# Revit family: Hitachi_RAS-70YHA4_RAS-80YHA4_1116
name_source: partatom
category: Mechanical Equipment
revit_build: Autodesk Revit 2013 (Build: 20120221_2030(x64)
units: mm (PartAtom-declared; Revit-internal decimal feet)

## types (2) — shared parameters
Depth = 250 mm  [stored 0.82021 ft]
Energy Star = Yes
Height = 300 mm
Manufacturer = Hitachi
Pip Connection Size - Liquid = 6.40 mm
Pipe Connection Size - Gas = 15.80 mm
Pipe Length (min./max.) = 3m to 30m
URL = www.temperzone.biz
Weight (kg) = 15
Width = 1100 mm

## per-type parameters (varying)
| type | Cooling Capacity | Cooling Range (kW) | Description | Heating Capacity | Heating Range (kW) | Model - Outdoor | Pipe Height (max.) |
| RAS-80YHA4 | 8 kW | 1.5 kW to 8.5 kW | Hitachi Wall Mounted 8.0kW Heatpump RAS-80YHA4 | 9 kW | 1.5 kW to 9.7 kW | RAC-80YHA4 | 20m |
| RAS-70YHA4 | 7 kW | 1.5 kW to 8.3 kW | Hitachi Wall Mounted 7.0kW Heatpump RAS-70YHA4 | 8 kW | 1.5 kW to 9.0 kW | RAC-70YHA4 | 20 |

note: column(s) folded — value = type name in every type: Model

note: [stored X ft] marks values corroborated as IEEE doubles in the binary element streams (Revit-internal decimal feet)

## geometry (parser evidence)
native form markers: Blend x4, Sweep x3
no freeform markers — native parametric forms only
